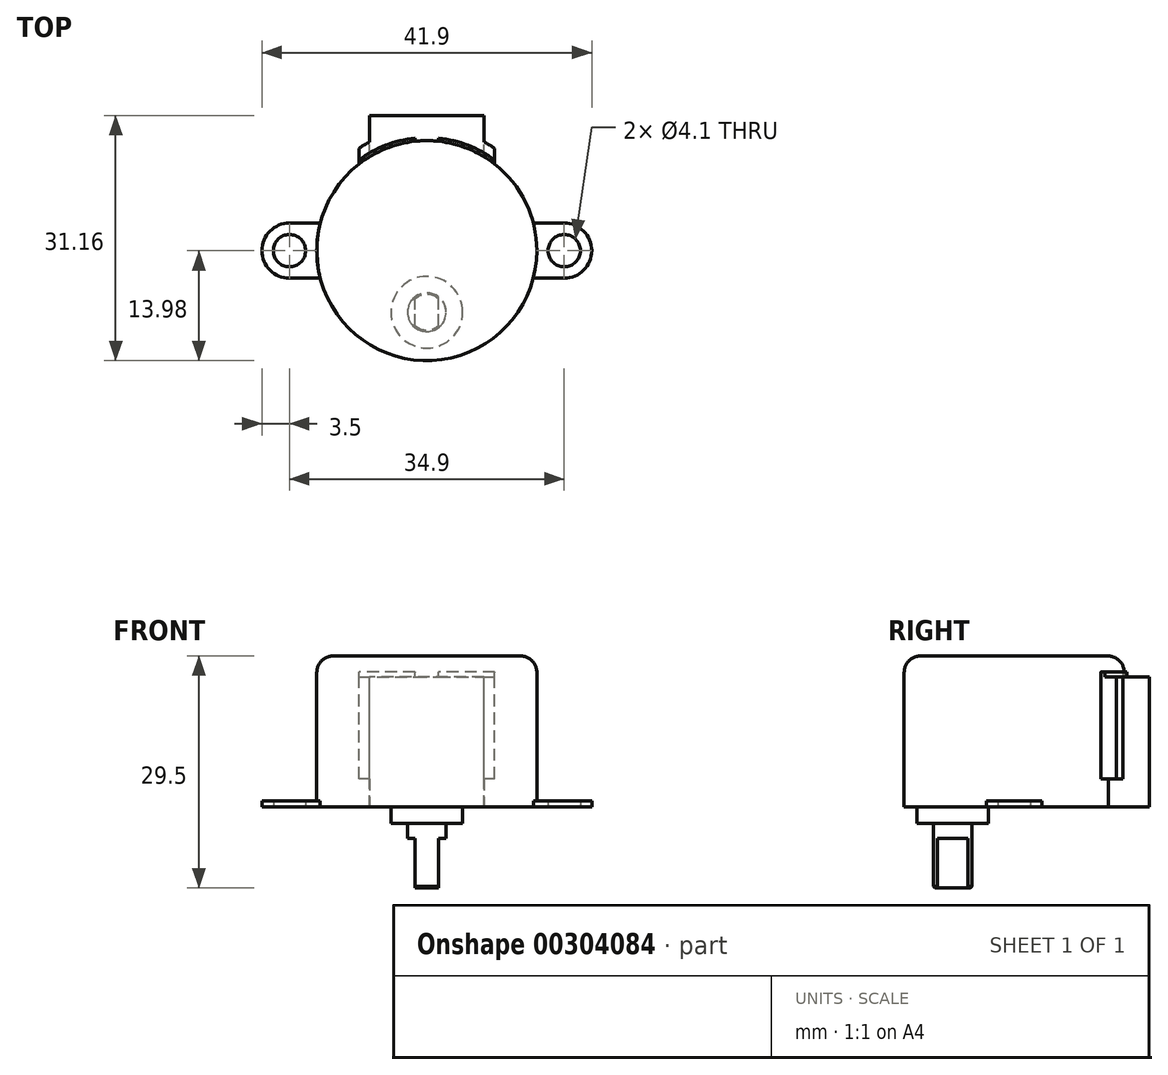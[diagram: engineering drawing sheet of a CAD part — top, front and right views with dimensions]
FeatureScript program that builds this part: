
annotation { "Feature Type Name" : "Feature", "Feature Type Description" : "" }
export const myFeature = defineFeature(function(context is Context, id is Id, definition is map)
    precondition{}
    {
        {
            var Q0;
            Q0=qCreatedBy(makeId("Top.planeOp"),FACE);
            var sketch = newSketch(context, id + "F0", { "sketchPlane" : qUnion([Q0])});
            skArc(sketch, "E0", {"start": v(13.53, 3.5) * mm, "mid": v(0, 13.97) * mm, "end": v(-13.53, 3.5) * mm});
            skLineSegment(sketch, "E1", {"start": v(0, 41.3) * mm, "end": v(0, -21.58) * mm, "construction": true});
            skLineSegment(sketch, "E2", {"start": v(0, 0) * mm, "end": v(20.95, 0) * mm, "construction": true});
            skLineSegment(sketch, "E3.0", {"start": v(13.53, -3.5) * mm, "end": v(17.45, -3.5) * mm});
            skLineSegment(sketch, "E4.0", {"start": v(13.53, 3.5) * mm, "end": v(17.45, 3.5) * mm});
            skCircle(sketch, "E5", {"center": v(17.45, 0) * mm, "radius": 2.05 * mm});
            skArc(sketch, "E6", {"start": v(17.45, -3.5) * mm, "mid": v(20.95, 0) * mm, "end": v(17.45, 3.5) * mm});
            skLineSegment(sketch, "E7.MirrorCS", {"start": v(-13.53, -3.5) * mm, "end": v(-17.45, -3.5) * mm});
            skLineSegment(sketch, "E8.MirrorCS", {"start": v(-13.53, 3.5) * mm, "end": v(-17.45, 3.5) * mm});
            skCircle(sketch, "E9.MirrorC", {"center": v(-17.45, 0) * mm, "radius": 2.05 * mm});
            skArc(sketch, "E10.MirrorCS", {"start": v(-17.45, -3.5) * mm, "mid": v(-20.95, 0) * mm, "end": v(-17.45, 3.5) * mm});
            skArc(sketch, "E11.trimOffspring", {"start": v(-13.53, -3.5) * mm, "mid": v(0, -13.97) * mm, "end": v(13.53, -3.5) * mm});
            skArc(sketch, "E12", {"start": v(-13.53, 3.5) * mm, "mid": v(-13.98, 0) * mm, "end": v(-13.53, -3.5) * mm});
            skArc(sketch, "E13.trimOffspring", {"start": v(13.53, -3.5) * mm, "mid": v(13.98, 0) * mm, "end": v(13.53, 3.5) * mm});
            skSolve(sketch);
        }
        {
            var Q0;
            Q0=makeQuery(id+"F0.imprint","IMPRINT",FACE,{"disambiguationData":[TD([[makeQuery(id+"F0.imprint","IMPRINT",EDGE,{"derivedFrom":sQuery(id+"F0.wireOp",EDGE,"E7.MirrorCS")}),-1.0]])]});
            var Q1;
            Q1=makeQuery(id+"F0.imprint","IMPRINT",FACE,{"disambiguationData":[TD([[makeQuery(id+"F0.imprint","IMPRINT",EDGE,{"derivedFrom":sQuery(id+"F0.wireOp",EDGE,"E3.0")}),1.0]])]});
            extrude(context, id + "F1", {"entities" : qUnion([Q0, Q1]), "depth" : 0.8 * mm});
        }
        {
            var Q0;
            Q0=makeQuery(id+"F0.imprint","IMPRINT",FACE,{"disambiguationData":[TD([[makeQuery(id+"F0.imprint","IMPRINT",EDGE,{"derivedFrom":sQuery(id+"F0.wireOp",EDGE,"E0")}),1.0]])]});
            extrude(context, id + "F2", {"entities" : qUnion([Q0]), "operationType" : NewBodyOperationType.ADD, "depth" : 19.2 * mm});
        }
        {
            var Q0;
            Q0=qCreatedBy(makeId("Top.planeOp"),FACE);
            var sketch = newSketch(context, id + "F3", { "sketchPlane" : qUnion([Q0])});
            skCircle(sketch, "E14", {"center": v(0, -7.82) * mm, "radius": 4.55 * mm});
            skCircle(sketch, "E15", {"center": v(0, -7.82) * mm, "radius": 2.45 * mm});
            skPoint(sketch, "E16", {"position": v(0, -3.27) * mm});
            skLineSegment(sketch, "E17.left", {"start": v(1.47, -9.78) * mm, "end": v(1.47, -5.87) * mm});
            skLineSegment(sketch, "E17.right", {"start": v(-1.48, -9.78) * mm, "end": v(-1.48, -5.87) * mm});
            skLineSegment(sketch, "E18", {"start": v(-1.48, -9.78) * mm, "end": v(1.47, -9.78) * mm, "construction": true});
            skLineSegment(sketch, "E19", {"start": v(-1.48, -5.87) * mm, "end": v(1.47, -5.87) * mm, "construction": true});
            skSolve(sketch);
        }
        {
            var Q0;
            Q0=makeQuery(id+"F3.imprint","IMPRINT",FACE,{"disambiguationData":[TD([[makeQuery(id+"F3.imprint","IMPRINT",EDGE,{"derivedFrom":sQuery(id+"F3.wireOp",EDGE,"E14")}),1.0]])]});
            extrude(context, id + "F4", {"entities" : qUnion([Q0]), "operationType" : NewBodyOperationType.ADD, "oppositeDirection" : true, "depth" : 2.1 * mm});
        }
        {
            var Q0;
            {var subQ0=sQuery(id+"F3.wireOp",EDGE,"E17.left");Q0=makeQuery(id+"F3.imprint","IMPRINT",FACE,{"disambiguationData":[TD([[makeQuery(id+"F3.imprint","IMPRINT",EDGE,{"derivedFrom":subQ0}),-1.0]])]});}
            var Q1;
            {var subQ0=sQuery(id+"F3.wireOp",EDGE,"E17.left");Q1=makeQuery(id+"F3.imprint","IMPRINT",FACE,{"disambiguationData":[TD([[makeQuery(id+"F3.imprint","IMPRINT",EDGE,{"derivedFrom":subQ0}),1.0]])]});}
            var Q2;
            {var subQ0=sQuery(id+"F3.wireOp",EDGE,"E17.right");Q2=makeQuery(id+"F3.imprint","IMPRINT",FACE,{"disambiguationData":[TD([[makeQuery(id+"F3.imprint","IMPRINT",EDGE,{"derivedFrom":subQ0}),1.0]])]});}
            extrude(context, id + "F5", {"entities" : qUnion([Q0, Q1, Q2]), "operationType" : NewBodyOperationType.ADD, "oppositeDirection" : true, "depth" : 4 * mm});
        }
        {
            var Q0;
            {var subQ0=sQuery(id+"F3.wireOp",EDGE,"E17.left");Q0=makeQuery(id+"F3.imprint","IMPRINT",FACE,{"disambiguationData":[TD([[makeQuery(id+"F3.imprint","IMPRINT",EDGE,{"derivedFrom":subQ0}),1.0]])]});}
            extrude(context, id + "F6", {"entities" : qUnion([Q0]), "operationType" : NewBodyOperationType.ADD, "oppositeDirection" : true, "depth" : 10.3 * mm});
        }
        {
            var Q0;
            Q0=qCreatedBy(makeId("Front.planeOp"),FACE);
            cPlane(context, id + "F7", {"entities" : qUnion([Q0]), "cplaneType" : CPlaneType.OFFSET, "offset" : (31.15 - 27.95 / 2) * mm, "oppositeDirection" : true, "width" : 150 * mm, "height" : 150 * mm});
        }
        {
            var Q0;
            Q0=qCreatedBy(id+"F7.planeOp",FACE);
            var sketch = newSketch(context, id + "F8", { "sketchPlane" : qUnion([Q0])});
            skLineSegment(sketch, "E20.0", {"start": v(13.53, 0) * mm, "end": v(-13.53, 0) * mm});
            skLineSegment(sketch, "E21.bottom", {"start": v(7.25, 0) * mm, "end": v(-7.25, 0) * mm});
            skLineSegment(sketch, "E21.top", {"start": v(7.25, 16.5) * mm, "end": v(-7.25, 16.5) * mm});
            skLineSegment(sketch, "E21.left", {"start": v(7.25, 0) * mm, "end": v(7.25, 16.5) * mm});
            skLineSegment(sketch, "E21.right", {"start": v(-7.25, 0) * mm, "end": v(-7.25, 16.5) * mm});
            skPoint(sketch, "E22", {"position": v(0, 0) * mm});
            skSolve(sketch);
        }
        {
            var Q0;
            Q0=qSketchRegion(id+"F8",true);
            var Q1;
            Q1=makeQuery(id+"F2.opExtrude","SWEPT_FACE",FACE,{"disambiguationData":[OSD([sQuery(id+"F0.wireOp",EDGE,"E0"),sQuery(id+"F0.wireOp",EDGE,"E11.trimOffspring"),sQuery(id+"F0.wireOp",EDGE,"E12"),sQuery(id+"F0.wireOp",EDGE,"E13.trimOffspring")])]});
            extrude(context, id + "F9", {"entities" : qUnion([Q0]), "operationType" : NewBodyOperationType.ADD, "endBound" : BoundingType.UP_TO_SURFACE, "endBoundEntityFace" : qUnion([Q1]), "depth" : 25 * mm});
        }
        {
            var Q0;
            Q0=makeQuery(id+"F2.opExtrude","CAP_FACE",FACE,{"disambiguationData":[OSD([sQuery(id+"F0.wireOp",EDGE,"E0"),sQuery(id+"F0.wireOp",EDGE,"E11.trimOffspring"),sQuery(id+"F0.wireOp",EDGE,"E12"),sQuery(id+"F0.wireOp",EDGE,"E13.trimOffspring")])],"isStart":false});
            cPlane(context, id + "F10", {"entities" : qUnion([Q0]), "cplaneType" : CPlaneType.OFFSET, "offset" : 2.05 * mm, "oppositeDirection" : true, "width" : 150 * mm, "height" : 150 * mm});
        }
        {
            var Q0;
            Q0=qCreatedBy(id+"F10.planeOp",FACE);
            var sketch = newSketch(context, id + "F11", { "sketchPlane" : qUnion([Q0])});
            skArc(sketch, "E23", {"start": v(8.62, 11.5) * mm, "mid": v(5.25, 13.38) * mm, "end": v(1.5, 14.3) * mm});
            skCircle(sketch, "E24.0", {"center": v(0, 0) * mm, "radius": 13.97 * mm});
            skLineSegment(sketch, "E25", {"start": v(8.62, 11) * mm, "end": v(8.62, 11.5) * mm});
            skLineSegment(sketch, "E26", {"start": v(-8.62, 11) * mm, "end": v(-8.62, 11.5) * mm});
            skLineSegment(sketch, "E27", {"start": v(-8.62, 11) * mm, "end": v(0, 11) * mm, "construction": true});
            skLineSegment(sketch, "E28", {"start": v(0, 11) * mm, "end": v(8.62, 11) * mm, "construction": true});
            skLineSegment(sketch, "E29", {"start": v(-8.62, 11.5) * mm, "end": v(-8.62, 13) * mm});
            skLineSegment(sketch, "E30.0", {"start": v(-7.25, 12.41) * mm, "end": v(-7.25, 13.82) * mm});
            skArc(sketch, "E31", {"start": v(-7.25, 13.82) * mm, "mid": v(-7.95, 13.43) * mm, "end": v(-8.62, 13) * mm});
            skLineSegment(sketch, "E32.MirrorCS", {"start": v(8.62, 11.5) * mm, "end": v(8.62, 13) * mm});
            skArc(sketch, "E33.MirrorCS", {"start": v(7.25, 13.82) * mm, "mid": v(7.95, 13.43) * mm, "end": v(8.62, 13) * mm});
            skLineSegment(sketch, "E34", {"start": v(7.25, 13.82) * mm, "end": v(7.25, 12.41) * mm});
            skPoint(sketch, "E35.orphan", {"position": v(-7.25, 11.95) * mm});
            skLineSegment(sketch, "E36", {"start": v(-1.5, 13.9) * mm, "end": v(-1.5, 14.3) * mm});
            skLineSegment(sketch, "E37", {"start": v(1.5, 13.9) * mm, "end": v(1.5, 14.3) * mm});
            skLineSegment(sketch, "E38", {"start": v(-1.5, 13.9) * mm, "end": v(1.5, 13.9) * mm, "construction": true});
            skPoint(sketch, "E39", {"position": v(0, 13.9) * mm});
            skLineSegment(sketch, "E40", {"start": v(0, 9.8) * mm, "end": v(0, 20.46) * mm, "construction": true});
            skArc(sketch, "E41.trimOffspring", {"start": v(-1.5, 14.3) * mm, "mid": v(-5.25, 13.38) * mm, "end": v(-8.62, 11.5) * mm});
            skSolve(sketch);
        }
        {
            var Q0;
            {var subQ0=sQuery(id+"F11.wireOp",EDGE,"E29");Q0=makeQuery(id+"F11.imprint","IMPRINT",FACE,{"disambiguationData":[TD([[makeQuery(id+"F11.imprint","IMPRINT",EDGE,{"derivedFrom":subQ0}),-1.0]])]});}
            var Q1;
            {var subQ0=sQuery(id+"F11.wireOp",EDGE,"E32.MirrorCS");Q1=makeQuery(id+"F11.imprint","IMPRINT",FACE,{"disambiguationData":[TD([[makeQuery(id+"F11.imprint","IMPRINT",EDGE,{"derivedFrom":subQ0}),1.0]])]});}
            var Q2;
            {var subQ3=sQuery(id+"F11.wireOp",EDGE,"E25");Q2=makeQuery(id+"F11.imprint","IMPRINT",FACE,{"disambiguationData":[TD([[makeQuery(id+"F11.imprint","IMPRINT",EDGE,{"derivedFrom":subQ3}),1.0]])]});}
            var Q3;
            {var subQ3=sQuery(id+"F11.wireOp",EDGE,"E26");Q3=makeQuery(id+"F11.imprint","IMPRINT",FACE,{"disambiguationData":[TD([[makeQuery(id+"F11.imprint","IMPRINT",EDGE,{"derivedFrom":subQ3}),-1.0]])]});}
            extrude(context, id + "F12", {"entities" : qUnion([Q0, Q1, Q2, Q3]), "operationType" : NewBodyOperationType.ADD, "oppositeDirection" : true, "depth" : 13.55 * mm});
        }
        {
            var Q0;
            {var subQ0=sQuery(id+"F11.wireOp",EDGE,"E29");Q0=makeQuery(id+"F11.imprint","IMPRINT",FACE,{"disambiguationData":[TD([[makeQuery(id+"F11.imprint","IMPRINT",EDGE,{"derivedFrom":subQ0}),-1.0]])]});}
            var Q1;
            {var subQ0=sQuery(id+"F11.wireOp",EDGE,"E32.MirrorCS");Q1=makeQuery(id+"F11.imprint","IMPRINT",FACE,{"disambiguationData":[TD([[makeQuery(id+"F11.imprint","IMPRINT",EDGE,{"derivedFrom":subQ0}),1.0]])]});}
            var Q2;
            Q2=makeQuery(id+"F9.opExtrude","SWEPT_FACE",FACE,{"disambiguationData":[OSD([sQuery(id+"F8.wireOp",EDGE,"E21.top")])]});
            extrude(context, id + "F13", {"entities" : qUnion([Q0, Q1]), "operationType" : NewBodyOperationType.REMOVE, "endBound" : BoundingType.UP_TO_SURFACE, "oppositeDirection" : true, "endBoundEntityFace" : qUnion([Q2]), "depth" : 1.5 * mm});
        }
        {
            var Q0;
            Q0=makeQuery(id+"F2.opExtrude","CAP_EDGE",EDGE,{"disambiguationData":[OSD([sQuery(id+"F0.wireOp",EDGE,"E0"),sQuery(id+"F0.wireOp",EDGE,"E11.trimOffspring"),sQuery(id+"F0.wireOp",EDGE,"E12"),sQuery(id+"F0.wireOp",EDGE,"E13.trimOffspring")])],"isStart":false});
            fillet(context, id + "F14", {"entities" : qUnion([Q0]), "radius" : 2.1 * mm, "tangentPropagation" : true, "allowEdgeOverflow" : false});
        }
        {
            var Q0;
            {var subQ0=sQuery(id+"F3.wireOp",EDGE,"E15");Q0=makeQuery(id+"F6.opExtrude","CAP_EDGE",EDGE,{"disambiguationData":[OSD([subQ0]),TDD([makeQuery(id+"F3.imprint","IMPRINT",EDGE,{"disambiguationData":[TD([[makeQuery(id+"F3.imprint","INTERSECT",VERTEX,{"disambiguationData":[OD(0.0)],"derivedFrom":[subQ0,sQuery(id+"F3.wireOp",EDGE,"E17.left")]}),1.0]])],"derivedFrom":subQ0})])],"isStart":false});}
            var Q1;
            {var subQ0=sQuery(id+"F3.wireOp",EDGE,"E15");Q1=makeQuery(id+"F6.opExtrude","CAP_EDGE",EDGE,{"disambiguationData":[OSD([subQ0]),TDD([makeQuery(id+"F3.imprint","IMPRINT",EDGE,{"disambiguationData":[TD([[makeQuery(id+"F3.imprint","INTERSECT",VERTEX,{"disambiguationData":[OD(1.0)],"derivedFrom":[subQ0,sQuery(id+"F3.wireOp",EDGE,"E17.left")]}),-1.0]])],"derivedFrom":subQ0})])],"isStart":false});}
            chamfer(context, id + "F15", {"entities" : qUnion([Q0, Q1]), "width" : 0.2 * mm, "tangentPropagation" : true});
        }
    });
